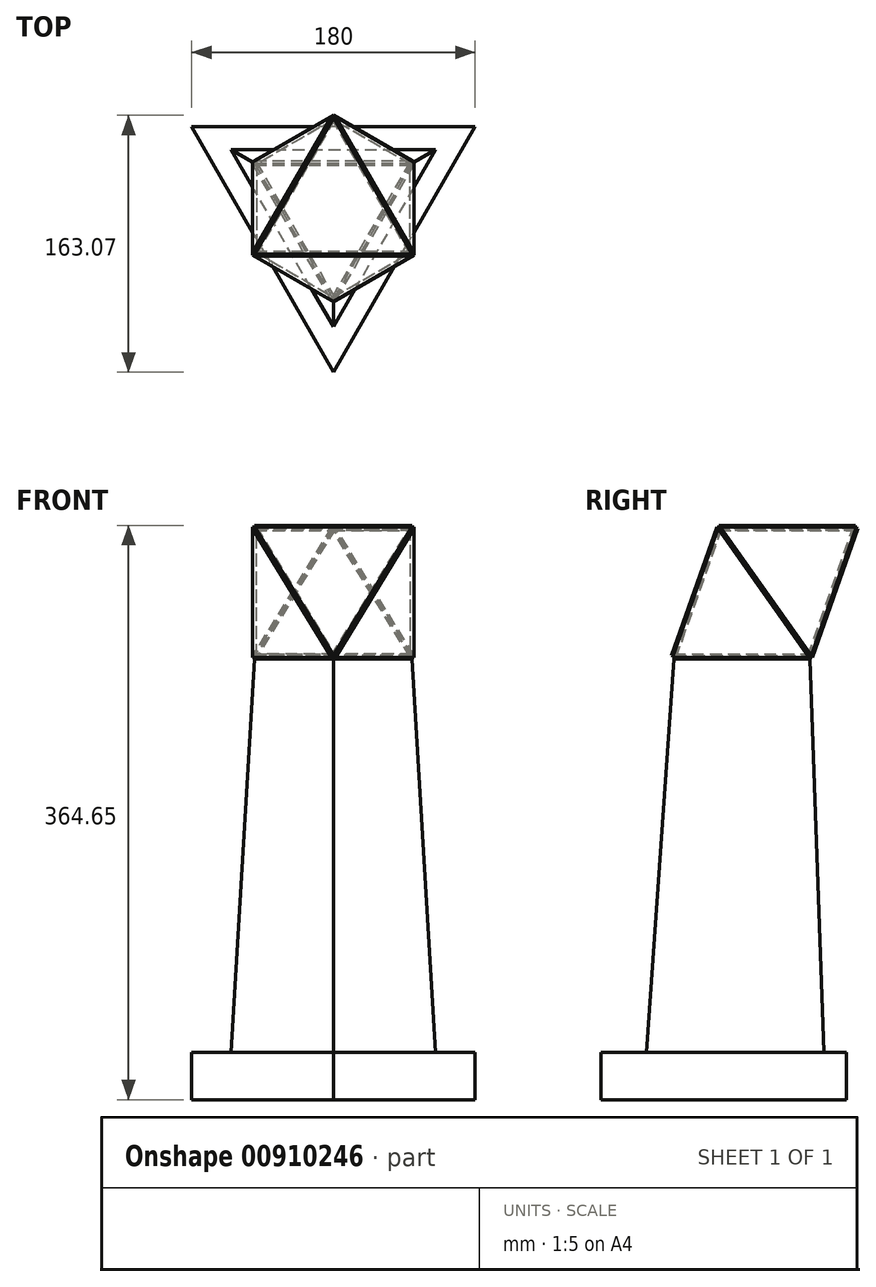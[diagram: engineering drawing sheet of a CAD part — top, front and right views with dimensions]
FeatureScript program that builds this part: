
annotation { "Feature Type Name" : "Feature", "Feature Type Description" : "" }
export const myFeature = defineFeature(function(context is Context, id is Id, definition is map)
    precondition{}
    {
        {
            var Q0;
            Q0=qCreatedBy(makeId("Top.planeOp"),FACE);
            var sketch = newSketch(context, id + "F0", { "sketchPlane" : qUnion([Q0])});
            skCircle(sketch, "E0.cCircle", {"center": v(0, 0) * mm, "radius": 28.87 * mm, "construction": true});
            skLineSegment(sketch, "E0.0", {"start": v(-50, 28.87) * mm, "end": v(50, 28.87) * mm});
            skLineSegment(sketch, "E0.1", {"start": v(50, 28.87) * mm, "end": v(0, -57.74) * mm});
            skLineSegment(sketch, "E0.2", {"start": v(0, -57.74) * mm, "end": v(-50, 28.87) * mm});
            skPoint(sketch, "E0.0.midPoint", {"position": v(0, 28.87) * mm});
            skSolve(sketch);
        }
        {
            var Q0;
            Q0=makeQuery(id+"F0.imprint","IMPRINT",FACE,{"disambiguationData":[TD([[makeQuery(id+"F0.imprint","IMPRINT",EDGE,{"derivedFrom":sQuery(id+"F0.wireOp",EDGE,"E0.0")}),-1.0]])]});
            extrude(context, id + "F1", {"entities" : qUnion([Q0]), "depth" : 3 * mm, "offsetDistance" : 25 * mm});
        }
        {
            var Q0;
            Q0=makeQuery(id+"F1.opExtrude","SWEPT_FACE",FACE,{"disambiguationData":[OSD([sQuery(id+"F0.wireOp",EDGE,"E0.2")])]});
            var sketch = newSketch(context, id + "F2", { "sketchPlane" : qUnion([Q0])});
            skLineSegment(sketch, "E1", {"start": v(-50, 1.5) * mm, "end": v(50, 1.5) * mm});
            skSolve(sketch);
        }
        {
            var Q0;
            Q0=makeQuery(id+"F1.opExtrude","SWEPT_BODY",BODY,{"disambiguationData":[OSD([sQuery(id+"F0.wireOp",EDGE,"E0.0"),sQuery(id+"F0.wireOp",EDGE,"E0.1"),sQuery(id+"F0.wireOp",EDGE,"E0.2")])]});
            transform(context, id + "F3", {"entities" : qUnion([Q0]), "transformType" : TransformType.TRANSLATION_3D, "dx" : 0 * mm, "dy" : 0 * mm, "dz" : 0 * mm, "makeCopy" : true});
        }
        {
            var Q0;
            Q0=makeQuery(id+"F3.opPattern","COPY",BODY,{"derivedFrom":makeQuery(id+"F1.opExtrude","SWEPT_BODY",BODY,{"disambiguationData":[OSD([sQuery(id+"F0.wireOp",EDGE,"E0.0"),sQuery(id+"F0.wireOp",EDGE,"E0.1"),sQuery(id+"F0.wireOp",EDGE,"E0.2")])]}),"instanceName":"1"});
            var Q1;
            Q1=sQuery(id+"F2.wireOp",EDGE,"E1");
            var Q2;
            Q2=sQuery(id+"F2.wireOp",EDGE,"E1");
            transform(context, id + "F4", {"entities" : qUnion([Q0]), "transformType" : TransformType.ROTATION, "transformAxis" : qUnion([Q2]), "angle" : 109.47 * degree, "makeCopy" : false});
        }
        {
            var Q0;
            Q0=makeQuery(id+"F1.opExtrude","SWEPT_BODY",BODY,{"disambiguationData":[OSD([sQuery(id+"F0.wireOp",EDGE,"E0.0"),sQuery(id+"F0.wireOp",EDGE,"E0.1"),sQuery(id+"F0.wireOp",EDGE,"E0.2")])]});
            transform(context, id + "F5", {"entities" : qUnion([Q0]), "transformType" : TransformType.TRANSLATION_3D, "dx" : 0 * mm, "dy" : 0 * mm, "dz" : 0 * mm, "makeCopy" : true});
        }
        {
            var Q0;
            Q0=makeQuery(id+"F1.opExtrude","SWEPT_FACE",FACE,{"disambiguationData":[OSD([sQuery(id+"F0.wireOp",EDGE,"E0.0")])]});
            var sketch = newSketch(context, id + "F6", { "sketchPlane" : qUnion([Q0])});
            skLineSegment(sketch, "E2", {"start": v(50, 1.5) * mm, "end": v(-50, 1.5) * mm});
            skSolve(sketch);
        }
        {
            var Q0;
            Q0=makeQuery(id+"F5.opPattern","COPY",BODY,{"derivedFrom":makeQuery(id+"F1.opExtrude","SWEPT_BODY",BODY,{"disambiguationData":[OSD([sQuery(id+"F0.wireOp",EDGE,"E0.0"),sQuery(id+"F0.wireOp",EDGE,"E0.1"),sQuery(id+"F0.wireOp",EDGE,"E0.2")])]}),"instanceName":"1"});
            var Q1;
            Q1=sQuery(id+"F6.wireOp",EDGE,"E2");
            var Q2;
            Q2=sQuery(id+"F6.wireOp",EDGE,"E2");
            transform(context, id + "F7", {"entities" : qUnion([Q0]), "transformType" : TransformType.ROTATION, "transformAxis" : qUnion([Q2]), "angle" : 109.47 * degree, "oppositeDirection" : true, "makeCopy" : false});
        }
        {
            var Q0;
            Q0=qCreatedBy(makeId("Front.planeOp"),FACE);
            var sketch = newSketch(context, id + "F8", { "sketchPlane" : qUnion([Q0])});
            skLineSegment(sketch, "E3", {"start": v(0, 0) * mm, "end": v(0, 75.98) * mm});
            skSolve(sketch);
        }
        {
            var Q0;
            Q0=makeQuery(id+"F3.opPattern","COPY",BODY,{"derivedFrom":makeQuery(id+"F1.opExtrude","SWEPT_BODY",BODY,{"disambiguationData":[OSD([sQuery(id+"F0.wireOp",EDGE,"E0.0"),sQuery(id+"F0.wireOp",EDGE,"E0.1"),sQuery(id+"F0.wireOp",EDGE,"E0.2")])]}),"instanceName":"1"});
            var Q1;
            Q1=sQuery(id+"F8.wireOp",EDGE,"E3");
            circularPattern(context, id + "F9", {"entities" : qUnion([Q0]), "axis" : qUnion([Q1]), "angle" : 360 * degree, "instanceCount" : 3, "equalSpace" : true});
        }
        {
            var Q0;
            Q0=makeQuery(id+"F5.opPattern","COPY",FACE,{"derivedFrom":makeQuery(id+"F1.opExtrude","SWEPT_FACE",FACE,{"disambiguationData":[OSD([sQuery(id+"F0.wireOp",EDGE,"E0.1")])]}),"instanceName":"1"});
            var sketch = newSketch(context, id + "F10", { "sketchPlane" : qUnion([Q0])});
            skLineSegment(sketch, "E4", {"start": v(21.03, -22.59) * mm, "end": v(50.3, 73.03) * mm});
            skSolve(sketch);
        }
        {
            var Q0;
            Q0=makeQuery(id+"F5.opPattern","COPY",BODY,{"derivedFrom":makeQuery(id+"F1.opExtrude","SWEPT_BODY",BODY,{"disambiguationData":[OSD([sQuery(id+"F0.wireOp",EDGE,"E0.0"),sQuery(id+"F0.wireOp",EDGE,"E0.1"),sQuery(id+"F0.wireOp",EDGE,"E0.2")])]}),"instanceName":"1"});
            var Q1;
            Q1=sQuery(id+"F10.wireOp",EDGE,"E4");
            transform(context, id + "F11", {"entities" : qUnion([Q0]), "transformType" : TransformType.ROTATION, "transformAxis" : qUnion([Q1]), "angle" : 109.47 * degree, "makeCopy" : false});
        }
        {
            var Q0;
            Q0=makeQuery(id+"F5.opPattern","COPY",BODY,{"derivedFrom":makeQuery(id+"F1.opExtrude","SWEPT_BODY",BODY,{"disambiguationData":[OSD([sQuery(id+"F0.wireOp",EDGE,"E0.0"),sQuery(id+"F0.wireOp",EDGE,"E0.1"),sQuery(id+"F0.wireOp",EDGE,"E0.2")])]}),"instanceName":"1"});
            var Q1;
            Q1=sQuery(id+"F8.wireOp",EDGE,"E3");
            circularPattern(context, id + "F12", {"entities" : qUnion([Q0]), "axis" : qUnion([Q1]), "angle" : 360 * degree, "instanceCount" : 3, "equalSpace" : true});
        }
        {
            var Q0;
            Q0=makeQuery(id+"F5.opPattern","COPY",FACE,{"derivedFrom":makeQuery(id+"F1.opExtrude","SWEPT_FACE",FACE,{"disambiguationData":[OSD([sQuery(id+"F0.wireOp",EDGE,"E0.2")])]}),"instanceName":"1"});
            var sketch = newSketch(context, id + "F13", { "sketchPlane" : qUnion([Q0])});
            skLineSegment(sketch, "E5", {"start": v(20.74, 71.33) * mm, "end": v(72.96, -13.95) * mm});
            skSolve(sketch);
        }
        {
            var Q0;
            Q0=makeQuery(id+"F5.opPattern","COPY",BODY,{"derivedFrom":makeQuery(id+"F1.opExtrude","SWEPT_BODY",BODY,{"disambiguationData":[OSD([sQuery(id+"F0.wireOp",EDGE,"E0.0"),sQuery(id+"F0.wireOp",EDGE,"E0.1"),sQuery(id+"F0.wireOp",EDGE,"E0.2")])]}),"instanceName":"1"});
            transform(context, id + "F14", {"entities" : qUnion([Q0]), "transformType" : TransformType.TRANSLATION_3D, "dx" : 0 * mm, "dy" : 0 * mm, "dz" : 0 * mm, "makeCopy" : true});
        }
        {
            var Q0;
            Q0=makeQuery(id+"F14.opPattern","COPY",BODY,{"derivedFrom":makeQuery(id+"F5.opPattern","COPY",BODY,{"derivedFrom":makeQuery(id+"F1.opExtrude","SWEPT_BODY",BODY,{"disambiguationData":[OSD([sQuery(id+"F0.wireOp",EDGE,"E0.0"),sQuery(id+"F0.wireOp",EDGE,"E0.1"),sQuery(id+"F0.wireOp",EDGE,"E0.2")])]}),"instanceName":"1"}),"instanceName":"1"});
            var Q1;
            Q1=sQuery(id+"F13.wireOp",EDGE,"E5");
            var Q2;
            Q2=sQuery(id+"F13.wireOp",EDGE,"E5");
            transform(context, id + "F15", {"entities" : qUnion([Q0]), "transformType" : TransformType.ROTATION, "transformAxis" : qUnion([Q2]), "angle" : 109.47 * degree, "oppositeDirection" : true, "makeCopy" : false});
        }
        {
            var Q0;
            Q0=qCreatedBy(makeId("Top.planeOp"),FACE);
            cPlane(context, id + "F16", {"entities" : qUnion([Q0]), "cplaneType" : CPlaneType.OFFSET, "offset" : 250 * mm, "oppositeDirection" : true, "width" : 150 * mm, "height" : 150 * mm});
        }
        {
            var Q0;
            Q0=qCreatedBy(id+"F16.planeOp",FACE);
            var sketch = newSketch(context, id + "F17", { "sketchPlane" : qUnion([Q0])});
            skCircle(sketch, "E6.cCircle", {"center": v(0, 0) * mm, "radius": 37.53 * mm, "construction": true});
            skLineSegment(sketch, "E6.0", {"start": v(65, 37.53) * mm, "end": v(0, -75.06) * mm});
            skLineSegment(sketch, "E6.1", {"start": v(0, -75.06) * mm, "end": v(-65, 37.53) * mm});
            skLineSegment(sketch, "E6.2", {"start": v(-65, 37.53) * mm, "end": v(65, 37.53) * mm});
            skPoint(sketch, "E6.0.midPoint", {"position": v(32.5, -18.76) * mm});
            skSolve(sketch);
        }
        {
            var Q0;
            Q0=makeQuery(id+"F1.opExtrude","CAP_FACE",FACE,{"disambiguationData":[OSD([sQuery(id+"F0.wireOp",EDGE,"E0.0"),sQuery(id+"F0.wireOp",EDGE,"E0.1"),sQuery(id+"F0.wireOp",EDGE,"E0.2")])],"isStart":true});
            var sketch = newSketch(context, id + "F18", { "sketchPlane" : qUnion([Q0])});
            skCircle(sketch, "E7.cCircle", {"center": v(0, 0) * mm, "radius": 28.87 * mm, "construction": true});
            skLineSegment(sketch, "E7.0", {"start": v(-50, -28.87) * mm, "end": v(0, 57.74) * mm});
            skLineSegment(sketch, "E7.1", {"start": v(0, 57.74) * mm, "end": v(50, -28.87) * mm});
            skLineSegment(sketch, "E7.2", {"start": v(50, -28.87) * mm, "end": v(-50, -28.87) * mm});
            skPoint(sketch, "E7.0.midPoint", {"position": v(-25, 14.43) * mm});
            skSolve(sketch);
        }
        {
            var Q1;
            Q1=makeQuery(id+"F18.imprint","IMPRINT",FACE,{"disambiguationData":[TD([[makeQuery(id+"F18.imprint","IMPRINT",EDGE,{"derivedFrom":sQuery(id+"F18.wireOp",EDGE,"E7.0")}),1.0]])]});
            var Q2;
            Q2=makeQuery(id+"F17.imprint","IMPRINT",FACE,{"disambiguationData":[TD([[makeQuery(id+"F17.imprint","IMPRINT",EDGE,{"derivedFrom":sQuery(id+"F17.wireOp",EDGE,"E6.0")}),-1.0]])]});
            loft(context, id + "F19", {"operationType" : NewBodyOperationType.ADD, "sheetProfilesArray" : [{ "sheetProfileEntities" : qUnion([Q1]) }, { "sheetProfileEntities" : qUnion([Q2]) }]});
        }
        {
            var Q0;
            Q0=makeQuery(id+"F19.opLoft","CAP_FACE",FACE,{"disambiguationData":[OSD([makeQuery(id+"F17.imprint","IMPRINT",FACE,{"disambiguationData":[TD([[makeQuery(id+"F17.imprint","IMPRINT",EDGE,{"derivedFrom":sQuery(id+"F17.wireOp",EDGE,"E6.0")}),-1.0]])]})])],"isStart":true});
            var sketch = newSketch(context, id + "F20", { "sketchPlane" : qUnion([Q0])});
            skCircle(sketch, "E8.cCircle", {"center": v(0, 0) * mm, "radius": 51.96 * mm, "construction": true});
            skLineSegment(sketch, "E8.0", {"start": v(-90, -51.96) * mm, "end": v(0, 103.92) * mm});
            skLineSegment(sketch, "E8.1", {"start": v(0, 103.92) * mm, "end": v(90, -51.96) * mm});
            skLineSegment(sketch, "E8.2", {"start": v(90, -51.96) * mm, "end": v(-90, -51.96) * mm});
            skPoint(sketch, "E8.0.midPoint", {"position": v(-45, 25.98) * mm});
            skSolve(sketch);
        }
        {
            var Q0;
            Q0=makeQuery(id+"F20.imprint","IMPRINT",FACE,{"disambiguationData":[TD([[makeQuery(id+"F20.imprint","IMPRINT",EDGE,{"derivedFrom":sQuery(id+"F20.wireOp",EDGE,"E8.0")}),-1.0]])]});
            var Q1;
            {var subQ0=sQuery(id+"F17.wireOp",EDGE,"E6.0");var subQ1=sQuery(id+"F17.wireOp",EDGE,"E6.1");var subQ2=makeQuery(id+"F17.imprint","INTERSECT",VERTEX,{"derivedFrom":[subQ0,subQ1]});var subQ3=sQuery(id+"F17.wireOp",EDGE,"E6.2");var subQ4=makeQuery(id+"F17.imprint","INTERSECT",VERTEX,{"derivedFrom":[subQ0,subQ3]});Q1=makeQuery(id+"F20.imprint","IMPRINT",FACE,{"disambiguationData":[TD([[makeQuery(id+"F20.imprint","IMPRINT",EDGE,{"derivedFrom":makeQuery(id+"F19.opLoft","MID_CAP_EDGE",EDGE,{"disambiguationData":[OSD([subQ0,subQ1,subQ3]),TDD([subQ4,subQ2,makeQuery(id+"F17.imprint","IMPRINT",EDGE,{"derivedFrom":subQ0})])],"capPos":1.0})}),1.0]])]});}
            extrude(context, id + "F21", {"entities" : qUnion([Q0, Q1]), "operationType" : NewBodyOperationType.ADD, "depth" : 30 * mm, "offsetDistance" : 25 * mm});
        }
    });
